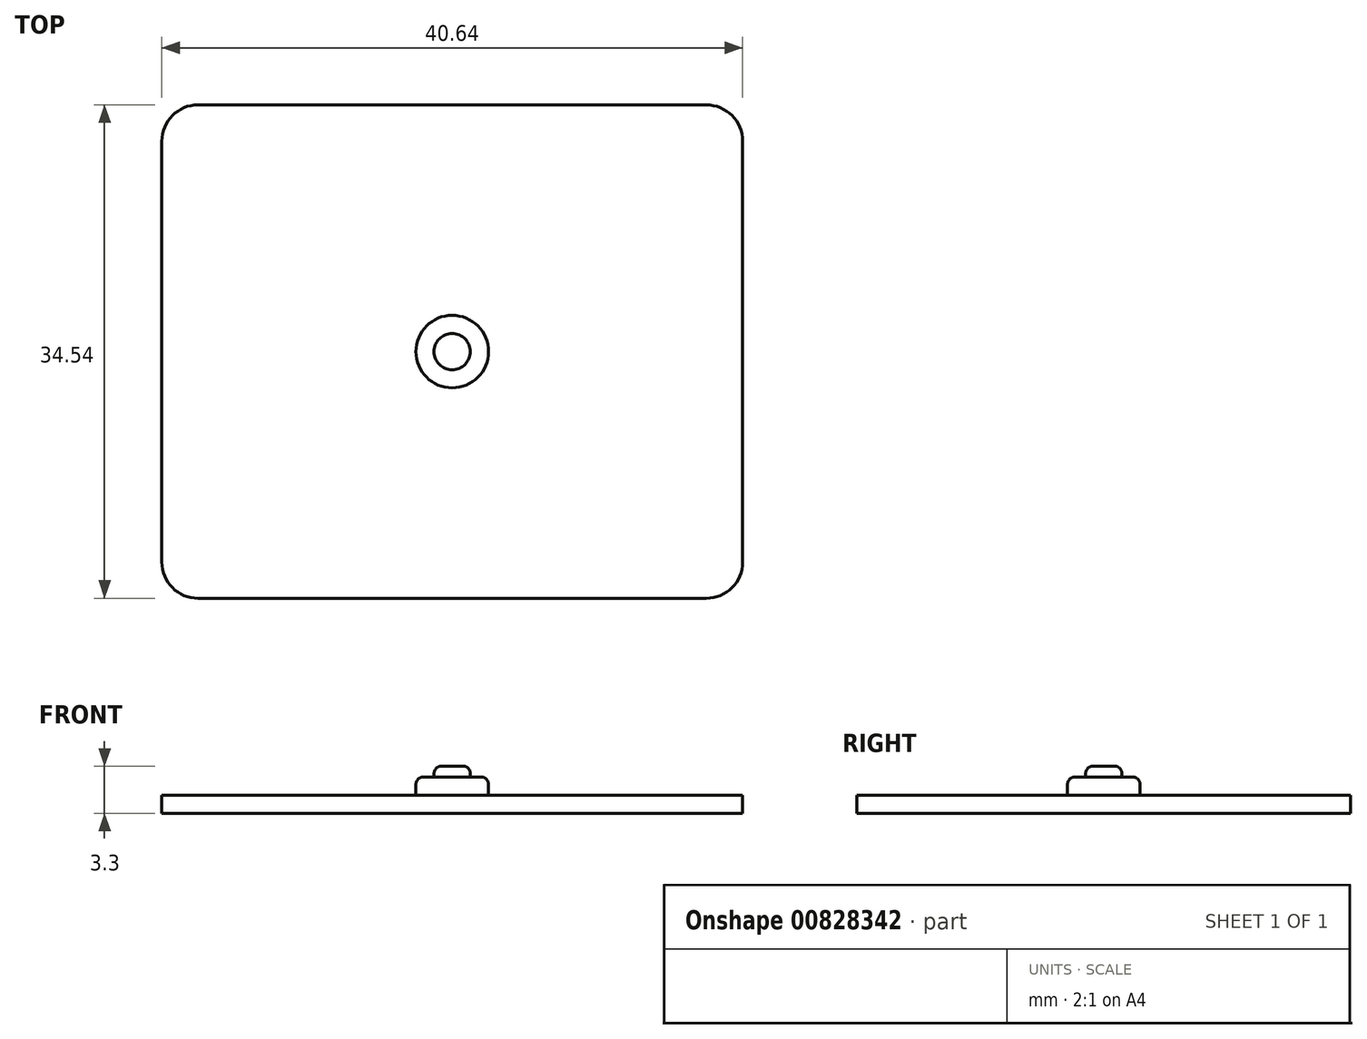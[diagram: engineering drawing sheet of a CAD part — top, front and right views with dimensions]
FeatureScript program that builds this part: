
annotation { "Feature Type Name" : "Feature", "Feature Type Description" : "" }
export const myFeature = defineFeature(function(context is Context, id is Id, definition is map)
    precondition{}
    {
        {
            var Q0;
            Q0=qCreatedBy(makeId("Top.planeOp"),FACE);
            var sketch = newSketch(context, id + "F0", { "sketchPlane" : qUnion([Q0])});
            skLineSegment(sketch, "E0.bottom", {"start": v(17.78, 17.27) * mm, "end": v(-17.78, 17.27) * mm});
            skLineSegment(sketch, "E0.top", {"start": v(17.78, -17.27) * mm, "end": v(-17.78, -17.27) * mm});
            skLineSegment(sketch, "E0.left", {"start": v(20.32, 14.73) * mm, "end": v(20.32, -14.73) * mm});
            skLineSegment(sketch, "E0.right", {"start": v(-20.32, 14.73) * mm, "end": v(-20.32, -14.73) * mm});
            skPoint(sketch, "E0.middle", {"position": v(0, 0) * mm});
            skPoint(sketch, "E1.visualSharp", {"position": v(-20.32, 17.27) * mm});
            skArc(sketch, "E1.filletArc", {"start": v(-17.78, 17.27) * mm, "mid": v(-19.58, 16.53) * mm, "end": v(-20.32, 14.73) * mm});
            skPoint(sketch, "E2.visualSharp", {"position": v(20.32, 17.27) * mm});
            skArc(sketch, "E2.filletArc", {"start": v(20.32, 14.73) * mm, "mid": v(19.58, 16.53) * mm, "end": v(17.78, 17.27) * mm});
            skPoint(sketch, "E3.visualSharp", {"position": v(20.32, -17.27) * mm});
            skArc(sketch, "E3.filletArc", {"start": v(17.78, -17.27) * mm, "mid": v(19.58, -16.53) * mm, "end": v(20.32, -14.73) * mm});
            skPoint(sketch, "E4.visualSharp", {"position": v(-20.32, -17.27) * mm});
            skArc(sketch, "E4.filletArc", {"start": v(-20.32, -14.73) * mm, "mid": v(-19.58, -16.53) * mm, "end": v(-17.78, -17.27) * mm});
            skSolve(sketch);
        }
        {
            var Q0;
            Q0 = qSketchRegion(id + "F0", true);
            extrude(context, id + "F1", {"entities" : qUnion([Q0]), "depth" : 1.27 * mm, "offsetDistance" : 25.4 * mm});
        }
        {
            var Q0;
            Q0=makeQuery(id+"F1.opExtrude","CAP_FACE",FACE,{"disambiguationData":[OSD([sQuery(id+"F0.wireOp",EDGE,"E0.bottom"),sQuery(id+"F0.wireOp",EDGE,"E0.top"),sQuery(id+"F0.wireOp",EDGE,"E0.left"),sQuery(id+"F0.wireOp",EDGE,"E0.right"),sQuery(id+"F0.wireOp",EDGE,"E1.filletArc"),sQuery(id+"F0.wireOp",EDGE,"E2.filletArc"),sQuery(id+"F0.wireOp",EDGE,"E3.filletArc"),sQuery(id+"F0.wireOp",EDGE,"E4.filletArc")])],"isStart":false});
            var sketch = newSketch(context, id + "F2", { "sketchPlane" : qUnion([Q0])});
            skCircle(sketch, "E5", {"center": v(0, 0) * mm, "radius": 2.54 * mm});
            skSolve(sketch);
        }
        {
            var Q0;
            Q0 = qSketchRegion(id + "F2", true);
            extrude(context, id + "F3", {"entities" : qUnion([Q0]), "operationType" : NewBodyOperationType.ADD, "depth" : 1.27 * mm, "offsetDistance" : 25.4 * mm});
        }
        {
            var Q0;
            Q0=makeQuery(id+"F3.opExtrude","CAP_FACE",FACE,{"disambiguationData":[OSD([sQuery(id+"F2.wireOp",EDGE,"E5")])],"isStart":false});
            var sketch = newSketch(context, id + "F4", { "sketchPlane" : qUnion([Q0])});
            skCircle(sketch, "E6", {"center": v(0, 0) * mm, "radius": 1.27 * mm});
            skSolve(sketch);
        }
        {
            var Q0;
            Q0 = qSketchRegion(id + "F4", true);
            extrude(context, id + "F5", {"entities" : qUnion([Q0]), "operationType" : NewBodyOperationType.ADD, "depth" : 0.76 * mm, "offsetDistance" : 25.4 * mm});
        }
        {
            var Q0;
            Q0=makeQuery(id+"F3.opExtrude","CAP_EDGE",EDGE,{"disambiguationData":[OSD([sQuery(id+"F2.wireOp",EDGE,"E5")])],"isStart":false});
            var Q1;
            Q1=makeQuery(id+"F5.opExtrude","CAP_EDGE",EDGE,{"disambiguationData":[OSD([sQuery(id+"F4.wireOp",EDGE,"E6")])],"isStart":false});
            fillet(context, id + "F6", {"entities" : qUnion([Q0, Q1]), "radius" : 0.5 * mm, "tangentPropagation" : true, "allowEdgeOverflow" : false});
        }
    });
